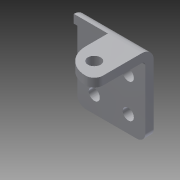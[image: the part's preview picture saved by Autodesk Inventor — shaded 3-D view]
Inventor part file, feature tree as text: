
AUTODESK INVENTOR PART (.ipt)
format: ipt  version: 2014 (Build 180170000, 170)  size: 219,136 bytes
history: native  units: in
note: dims shown in document units (in); Inventor stores cm internally (conversion verified against a paired STEP export)
features: sheet_metal_op x4, sketch x3, other x3, fillet x2, extrude x1
ambient origin geometry x8: Origin, YZ Plane, XZ Plane, XY Plane, X Axis, Y Axis, Z Axis, Center Point
bodies: Solid1 (feature_tree)
feature tree (13):
  sheet_metal_op  "Face1"
  sheet_metal_op  "Flange1"
  extrude  "Extrusion1"  Depth=1.0in
  fillet  "Fillet1"  Radius=0.164in
  fillet  "Fillet2"  Radius=0.25in
  sketch  "Sketch1"  dims[d0=1.0in d1=1.0in d2=0.164in d3=0.25in]
  other  "Plate1"
  sketch  "Sketch2"  dims[d4=0.25in]
  other  "Plate2"
  sheet_metal_op  "Bend1"
  sheet_metal_op  "Corner1"
  sketch  "Sketch3"  dims[d5=0.7874in d7=0.5in d8=0.7874in d10=0.5in d13=0.125in d14=0.125in d15=0.0625in d16=0.25in d17=0.125in d18=0.875in d19=90.0deg d20=0.05in d21=0.5in d22=0.125in d23=0.125in d24=0.187in d25=0.25in d26=0.25in d27=0.375in d28=0.125in d29=0.5in d30=1.0in d31=0.0in d32=0.125in d33=0.125in]
  other  "Definition1"
